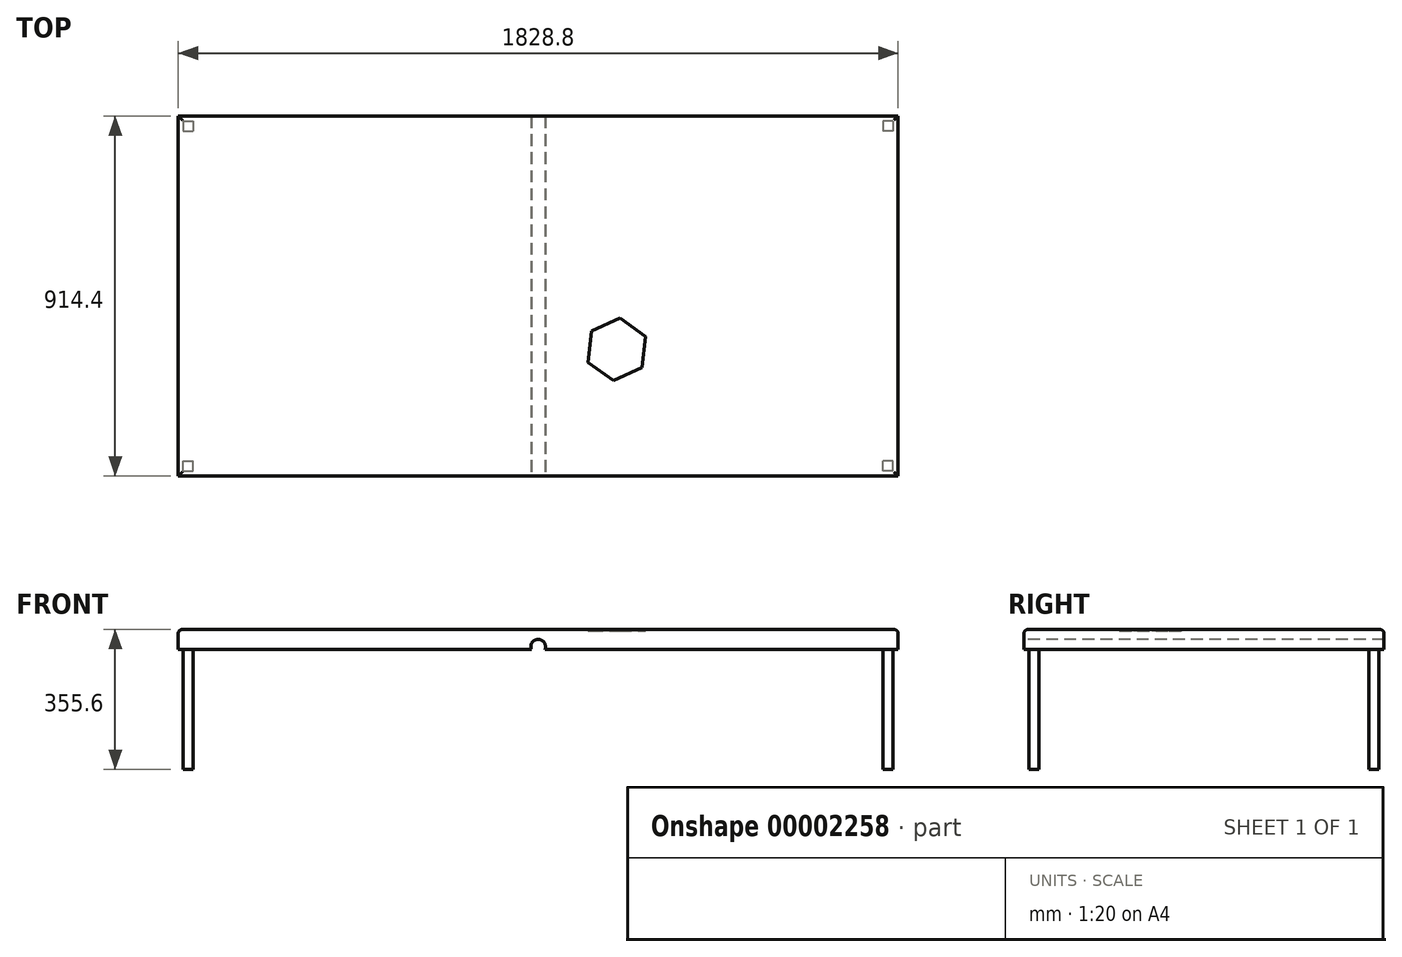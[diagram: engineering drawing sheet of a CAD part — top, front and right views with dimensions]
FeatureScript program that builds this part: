
annotation { "Feature Type Name" : "Feature", "Feature Type Description" : "" }
export const myFeature = defineFeature(function(context is Context, id is Id, definition is map)
    precondition{}
    {
        {
            var Q0;
            Q0=qCreatedBy(makeId("Top.planeOp"),FACE);
            var sketch = newSketch(context, id + "F0", { "sketchPlane" : qUnion([Q0])});
            skLineSegment(sketch, "E0.bottom", {"start": v(914.4, -457.2) * mm, "end": v(-914.4, -457.2) * mm});
            skLineSegment(sketch, "E0.top", {"start": v(914.4, 457.2) * mm, "end": v(-914.4, 457.2) * mm});
            skLineSegment(sketch, "E0.left", {"start": v(914.4, -457.2) * mm, "end": v(914.4, 457.2) * mm});
            skLineSegment(sketch, "E0.right", {"start": v(-914.4, -457.2) * mm, "end": v(-914.4, 457.2) * mm});
            skPoint(sketch, "E0.middle", {"position": v(0, 0) * mm});
            skSolve(sketch);
        }
        {
            var Q0;
            Q0=makeQuery(id+"F0.imprint","IMPRINT",FACE,{"disambiguationData":[TD([[makeQuery(id+"F0.imprint","IMPRINT",EDGE,{"derivedFrom":sQuery(id+"F0.wireOp",EDGE,"E0.bottom")}),-1.0]])]});
            extrude(context, id + "F1", {"entities" : qUnion([Q0]), "depth" : 50.8 * mm, "offsetDistance" : 25 * mm});
        }
        {
            var Q0;
            Q0=makeQuery(id+"F1.opExtrude","CAP_FACE",FACE,{"disambiguationData":[OSD([sQuery(id+"F0.wireOp",EDGE,"E0.bottom"),sQuery(id+"F0.wireOp",EDGE,"E0.top"),sQuery(id+"F0.wireOp",EDGE,"E0.left"),sQuery(id+"F0.wireOp",EDGE,"E0.right")])],"isStart":true});
            var sketch = newSketch(context, id + "F2", { "sketchPlane" : qUnion([Q0])});
            skLineSegment(sketch, "E1.bottom", {"start": v(901.7, 444.5) * mm, "end": v(876.3, 444.5) * mm});
            skLineSegment(sketch, "E1.top", {"start": v(901.7, 419.1) * mm, "end": v(876.3, 419.1) * mm});
            skLineSegment(sketch, "E1.left", {"start": v(901.7, 444.5) * mm, "end": v(901.7, 419.1) * mm});
            skLineSegment(sketch, "E1.right", {"start": v(876.3, 444.5) * mm, "end": v(876.3, 419.1) * mm});
            skLineSegment(sketch, "E2", {"start": v(0, 457.2) * mm, "end": v(0, -457.2) * mm, "construction": true});
            skLineSegment(sketch, "E3", {"start": v(914.4, 0) * mm, "end": v(-914.4, 0) * mm, "construction": true});
            skLineSegment(sketch, "E4.MirrorCS", {"start": v(-901.7, 444.5) * mm, "end": v(-876.3, 444.5) * mm});
            skLineSegment(sketch, "E5.MirrorCS", {"start": v(-901.7, 444.5) * mm, "end": v(-901.7, 419.1) * mm});
            skLineSegment(sketch, "E6.MirrorCS", {"start": v(-901.7, 419.1) * mm, "end": v(-876.3, 419.1) * mm});
            skLineSegment(sketch, "E7.MirrorCS", {"start": v(-876.3, 444.5) * mm, "end": v(-876.3, 419.1) * mm});
            skLineSegment(sketch, "E8.MirrorCS", {"start": v(-901.7, -444.5) * mm, "end": v(-876.3, -444.5) * mm});
            skLineSegment(sketch, "E9.MirrorCS", {"start": v(-876.3, -444.5) * mm, "end": v(-876.3, -419.1) * mm});
            skLineSegment(sketch, "E10.MirrorCS", {"start": v(-901.7, -419.1) * mm, "end": v(-876.3, -419.1) * mm});
            skLineSegment(sketch, "E11.MirrorCS", {"start": v(-901.7, -444.5) * mm, "end": v(-901.7, -419.1) * mm});
            skLineSegment(sketch, "E12.MirrorCS", {"start": v(901.7, -444.5) * mm, "end": v(901.7, -419.1) * mm});
            skLineSegment(sketch, "E13.MirrorCS", {"start": v(901.7, -444.5) * mm, "end": v(876.3, -444.5) * mm});
            skLineSegment(sketch, "E14.MirrorCS", {"start": v(876.3, -444.5) * mm, "end": v(876.3, -419.1) * mm});
            skLineSegment(sketch, "E15.MirrorCS", {"start": v(901.7, -419.1) * mm, "end": v(876.3, -419.1) * mm});
            skSolve(sketch);
        }
        {
            var Q0;
            Q0=makeQuery(id+"F2.imprint","IMPRINT",FACE,{"disambiguationData":[TD([[makeQuery(id+"F2.imprint","IMPRINT",EDGE,{"derivedFrom":sQuery(id+"F2.wireOp",EDGE,"E1.bottom")}),1.0]])]});
            var Q1;
            Q1=makeQuery(id+"F2.imprint","IMPRINT",FACE,{"disambiguationData":[TD([[makeQuery(id+"F2.imprint","IMPRINT",EDGE,{"derivedFrom":sQuery(id+"F2.wireOp",EDGE,"E4.MirrorCS")}),-1.0]])]});
            var Q2;
            Q2=makeQuery(id+"F2.imprint","IMPRINT",FACE,{"disambiguationData":[TD([[makeQuery(id+"F2.imprint","IMPRINT",EDGE,{"derivedFrom":sQuery(id+"F2.wireOp",EDGE,"E8.MirrorCS")}),1.0]])]});
            var Q3;
            Q3=makeQuery(id+"F2.imprint","IMPRINT",FACE,{"disambiguationData":[TD([[makeQuery(id+"F2.imprint","IMPRINT",EDGE,{"derivedFrom":sQuery(id+"F2.wireOp",EDGE,"E12.MirrorCS")}),1.0]])]});
            extrude(context, id + "F3", {"entities" : qUnion([Q0, Q1, Q2, Q3]), "operationType" : NewBodyOperationType.ADD, "depth" : 304.8 * mm, "offsetDistance" : 25 * mm});
        }
        {
            var Q0;
            Q0=makeQuery(id+"F1.opExtrude","SWEPT_FACE",FACE,{"disambiguationData":[OSD([sQuery(id+"F0.wireOp",EDGE,"E0.bottom")])]});
            var sketch = newSketch(context, id + "F4", { "sketchPlane" : qUnion([Q0])});
            skCircle(sketch, "E16", {"center": v(0, 7.02) * mm, "radius": 18.65 * mm});
            skPoint(sketch, "E16.centerSnap0", {"position": v(0, 0) * mm});
            skSolve(sketch);
        }
        {
            var Q0;
            {var subQ0=sQuery(id+"F4.wireOp",EDGE,"E16");var subQ1=makeQuery(id+"F1.opExtrude","CAP_EDGE",EDGE,{"disambiguationData":[OSD([sQuery(id+"F0.wireOp",EDGE,"E0.bottom")])],"isStart":true});var subQ2=makeQuery(id+"F4.imprint","INTERSECT",VERTEX,{"disambiguationData":[OD(0.0)],"derivedFrom":[subQ1,subQ0]});Q0=makeQuery(id+"F4.imprint","IMPRINT",FACE,{"disambiguationData":[TD([[makeQuery(id+"F4.imprint","IMPRINT",EDGE,{"disambiguationData":[TD([[subQ2,-1.0]])],"derivedFrom":subQ0}),1.0]])]});}
            var Q1;
            {var subQ0=sQuery(id+"F4.wireOp",EDGE,"E16");var subQ1=makeQuery(id+"F1.opExtrude","CAP_EDGE",EDGE,{"disambiguationData":[OSD([sQuery(id+"F0.wireOp",EDGE,"E0.bottom")])],"isStart":true});var subQ2=makeQuery(id+"F4.imprint","INTERSECT",VERTEX,{"disambiguationData":[OD(0.0)],"derivedFrom":[subQ1,subQ0]});Q1=makeQuery(id+"F4.imprint","IMPRINT",FACE,{"disambiguationData":[TD([[makeQuery(id+"F4.imprint","IMPRINT",EDGE,{"disambiguationData":[TD([[subQ2,1.0]])],"derivedFrom":subQ0}),1.0]])]});}
            extrude(context, id + "F5", {"entities" : qUnion([Q0, Q1]), "operationType" : NewBodyOperationType.REMOVE, "endBound" : BoundingType.UP_TO_NEXT, "oppositeDirection" : true, "depth" : 25 * mm, "offsetDistance" : 25 * mm});
        }
        {
            var Q0;
            Q0=makeQuery(id+"F1.opExtrude","CAP_EDGE",EDGE,{"disambiguationData":[OSD([sQuery(id+"F0.wireOp",EDGE,"E0.bottom")])],"isStart":false});
            var Q1;
            Q1=makeQuery(id+"F1.opExtrude","CAP_EDGE",EDGE,{"disambiguationData":[OSD([sQuery(id+"F0.wireOp",EDGE,"E0.left")])],"isStart":false});
            var Q2;
            Q2=makeQuery(id+"F1.opExtrude","CAP_EDGE",EDGE,{"disambiguationData":[OSD([sQuery(id+"F0.wireOp",EDGE,"E0.top")])],"isStart":false});
            var Q3;
            Q3=makeQuery(id+"F1.opExtrude","CAP_EDGE",EDGE,{"disambiguationData":[OSD([sQuery(id+"F0.wireOp",EDGE,"E0.right")])],"isStart":false});
            fillet(context, id + "F6", {"entities" : qUnion([Q0, Q1, Q2, Q3]), "tangentPropagation" : true, "radius" : 10 * mm, "defaultsChanged" : true, "vertexSettings" : [], "allowEdgeOverflow" : false});
        }
        {
            var Q0;
            Q0=makeQuery(id+"F1.opExtrude","CAP_FACE",FACE,{"disambiguationData":[OSD([sQuery(id+"F0.wireOp",EDGE,"E0.bottom"),sQuery(id+"F0.wireOp",EDGE,"E0.top"),sQuery(id+"F0.wireOp",EDGE,"E0.left"),sQuery(id+"F0.wireOp",EDGE,"E0.right")])],"isStart":false});
            var sketch = newSketch(context, id + "F7", { "sketchPlane" : qUnion([Q0])});
            skCircle(sketch, "E17.cCircle", {"center": v(0, 154.5) * mm, "radius": 176.97 * mm, "construction": true});
            skLineSegment(sketch, "E17.0", {"start": v(162.42, 226.06) * mm, "end": v(171.45, 200.43) * mm});
            skLineSegment(sketch, "E17.1", {"start": v(171.45, 200.43) * mm, "end": v(176.45, 173.72) * mm});
            skLineSegment(sketch, "E17.2", {"start": v(176.45, 173.72) * mm, "end": v(177.32, 146.56) * mm});
            skLineSegment(sketch, "E17.3", {"start": v(177.32, 146.56) * mm, "end": v(174.03, 119.58) * mm});
            skLineSegment(sketch, "E17.4", {"start": v(174.03, 119.58) * mm, "end": v(166.66, 93.43) * mm});
            skLineSegment(sketch, "E17.5", {"start": v(166.66, 93.43) * mm, "end": v(155.38, 68.7) * mm});
            skLineSegment(sketch, "E17.6", {"start": v(155.38, 68.7) * mm, "end": v(140.47, 45.99) * mm});
            skLineSegment(sketch, "E17.7", {"start": v(140.47, 45.99) * mm, "end": v(122.26, 25.82) * mm});
            skLineSegment(sketch, "E17.8", {"start": v(122.26, 25.82) * mm, "end": v(101.18, 8.66) * mm});
            skLineSegment(sketch, "E17.9", {"start": v(101.18, 8.66) * mm, "end": v(77.74, -5.07) * mm});
            skLineSegment(sketch, "E17.10", {"start": v(77.74, -5.07) * mm, "end": v(52.47, -15.07) * mm});
            skLineSegment(sketch, "E17.11", {"start": v(52.47, -15.07) * mm, "end": v(25.97, -21.1) * mm});
            skLineSegment(sketch, "E17.12", {"start": v(25.97, -21.1) * mm, "end": v(-1.14, -23) * mm});
            skLineSegment(sketch, "E17.13", {"start": v(-1.14, -23) * mm, "end": v(-28.22, -20.74) * mm});
            skLineSegment(sketch, "E17.14", {"start": v(-28.22, -20.74) * mm, "end": v(-54.64, -14.38) * mm});
            skLineSegment(sketch, "E17.15", {"start": v(-54.64, -14.38) * mm, "end": v(-79.77, -4.06) * mm});
            skLineSegment(sketch, "E17.16", {"start": v(-79.77, -4.06) * mm, "end": v(-103.04, 9.97) * mm});
            skLineSegment(sketch, "E17.17", {"start": v(-103.04, 9.97) * mm, "end": v(-123.9, 27.4) * mm});
            skLineSegment(sketch, "E17.18", {"start": v(-123.9, 27.4) * mm, "end": v(-141.85, 47.8) * mm});
            skLineSegment(sketch, "E17.19", {"start": v(-141.85, 47.8) * mm, "end": v(-156.47, 70.7) * mm});
            skLineSegment(sketch, "E17.20", {"start": v(-156.47, 70.7) * mm, "end": v(-167.43, 95.57) * mm});
            skLineSegment(sketch, "E17.21", {"start": v(-167.43, 95.57) * mm, "end": v(-174.46, 121.82) * mm});
            skLineSegment(sketch, "E17.22", {"start": v(-174.46, 121.82) * mm, "end": v(-177.4, 148.83) * mm});
            skLineSegment(sketch, "E17.23", {"start": v(-177.4, 148.83) * mm, "end": v(-176.19, 175.98) * mm});
            skLineSegment(sketch, "E17.24", {"start": v(-176.19, 175.98) * mm, "end": v(-170.84, 202.62) * mm});
            skLineSegment(sketch, "E17.25", {"start": v(-170.84, 202.62) * mm, "end": v(-161.5, 228.13) * mm});
            skLineSegment(sketch, "E17.26", {"start": v(-161.5, 228.13) * mm, "end": v(-148.36, 251.92) * mm});
            skLineSegment(sketch, "E17.27", {"start": v(-148.36, 251.92) * mm, "end": v(-131.75, 273.43) * mm});
            skLineSegment(sketch, "E17.28", {"start": v(-131.75, 273.43) * mm, "end": v(-112.05, 292.15) * mm});
            skLineSegment(sketch, "E17.29", {"start": v(-112.05, 292.15) * mm, "end": v(-89.72, 307.64) * mm});
            skLineSegment(sketch, "E17.30", {"start": v(-89.72, 307.64) * mm, "end": v(-65.3, 319.54) * mm});
            skLineSegment(sketch, "E17.31", {"start": v(-65.3, 319.54) * mm, "end": v(-39.33, 327.57) * mm});
            skLineSegment(sketch, "E17.32", {"start": v(-39.33, 327.57) * mm, "end": v(-12.45, 331.55) * mm});
            skLineSegment(sketch, "E17.33", {"start": v(-12.45, 331.55) * mm, "end": v(14.72, 331.37) * mm});
            skLineSegment(sketch, "E17.34", {"start": v(14.72, 331.37) * mm, "end": v(41.55, 327.05) * mm});
            skLineSegment(sketch, "E17.35", {"start": v(41.55, 327.05) * mm, "end": v(67.4, 318.69) * mm});
            skLineSegment(sketch, "E17.36", {"start": v(67.4, 318.69) * mm, "end": v(91.68, 306.48) * mm});
            skLineSegment(sketch, "E17.37", {"start": v(91.68, 306.48) * mm, "end": v(113.8, 290.7) * mm});
            skLineSegment(sketch, "E17.38", {"start": v(113.8, 290.7) * mm, "end": v(133.26, 271.73) * mm});
            skLineSegment(sketch, "E17.39", {"start": v(133.26, 271.73) * mm, "end": v(149.6, 250.02) * mm});
            skLineSegment(sketch, "E17.40", {"start": v(149.6, 250.02) * mm, "end": v(162.42, 226.06) * mm});
            skPoint(sketch, "E17.0.midPoint", {"position": v(166.94, 213.24) * mm});
            skCircle(sketch, "E18.cCircle", {"center": v(199.73, -135.6) * mm, "radius": 68.98 * mm, "construction": true});
            skLineSegment(sketch, "E18.0", {"start": v(207.71, -56.35) * mm, "end": v(272.36, -102.88) * mm});
            skLineSegment(sketch, "E18.1", {"start": v(272.36, -102.88) * mm, "end": v(264.38, -182.14) * mm});
            skLineSegment(sketch, "E18.2", {"start": v(264.38, -182.14) * mm, "end": v(191.76, -214.85) * mm});
            skLineSegment(sketch, "E18.3", {"start": v(191.76, -214.85) * mm, "end": v(127.11, -168.32) * mm});
            skLineSegment(sketch, "E18.4", {"start": v(127.11, -168.32) * mm, "end": v(135.09, -89.07) * mm});
            skLineSegment(sketch, "E18.5", {"start": v(135.09, -89.07) * mm, "end": v(207.71, -56.35) * mm});
            skPoint(sketch, "E18.0.midPoint", {"position": v(240.03, -79.62) * mm});
            skSolve(sketch);
        }
        {
            var Q0;
            Q0=makeQuery(id+"F7.imprint","IMPRINT",FACE,{"disambiguationData":[TD([[makeQuery(id+"F7.imprint","IMPRINT",EDGE,{"derivedFrom":sQuery(id+"F7.wireOp",EDGE,"E18.0")}),-1.0]])]});
            extrude(context, id + "F8", {"entities" : qUnion([Q0]), "operationType" : NewBodyOperationType.REMOVE, "oppositeDirection" : true, "depth" : 4 * mm, "offsetDistance" : 25 * mm});
        }
    });
